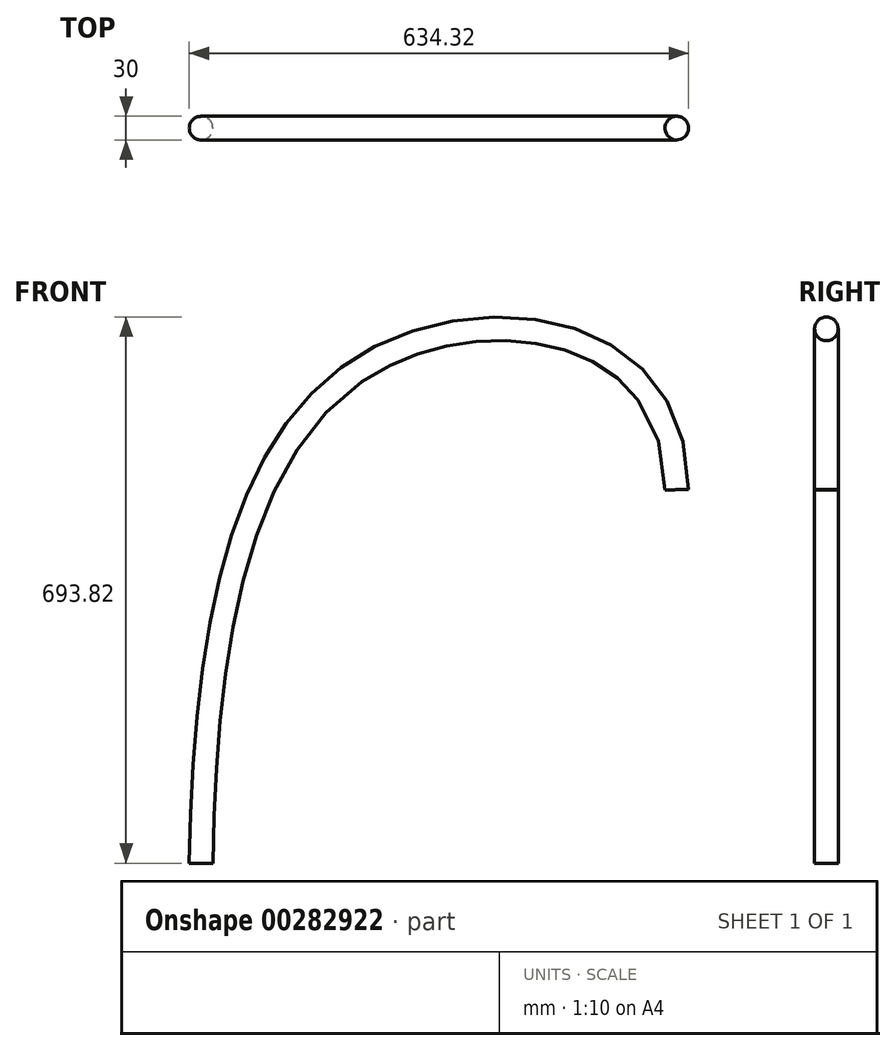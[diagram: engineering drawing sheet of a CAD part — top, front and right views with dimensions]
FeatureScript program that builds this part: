
annotation { "Feature Type Name" : "Feature", "Feature Type Description" : "" }
export const myFeature = defineFeature(function(context is Context, id is Id, definition is map)
    precondition{}
    {
        {
            var Q0;
            Q0=qCreatedBy(makeId("Front.planeOp"),FACE);
            var sketch = newSketch(context, id + "F0", { "sketchPlane" : qUnion([Q0])});
            skFitSpline(sketch, "E0", {"points": [v(0, 0) * mm, v(-380.97, 166.33) * mm, v(-604.32, -474.46) * mm], "startDerivative": vector(0, 1443.01) * mm, "endDerivative": vector(-27.43, -1426.3) * mm});
            skFitSpline(sketch, "E1.0", {"points": [v(-10, 0) * mm, v(-10, 14.5) * mm, v(-12.31, 41.6) * mm, v(-21.9, 76.83) * mm, v(-36.86, 106.96) * mm, v(-56.54, 132.32) * mm, v(-80.38, 153.2) * mm, v(-107.82, 169.76) * mm, v(-138.25, 182.1) * mm, v(-170.98, 190.29) * mm, v(-205.32, 194.42) * mm, v(-240.53, 194.62) * mm, v(-275.86, 191) * mm, v(-310.59, 183.71) * mm, v(-338.4, 174.72) * mm, v(-359.62, 165.86) * mm, v(-374.91, 158.41) * mm, v(-389.5, 150.17) * mm, v(-408.1, 138.15) * mm, v(-429.71, 121.23) * mm, v(-453.24, 98.05) * mm, v(-481.55, 63.5) * mm, v(-511.53, 13.9) * mm, v(-539.67, -54.5) * mm, v(-560.85, -130.24) * mm, v(-575.98, -211.72) * mm, v(-586, -297.36) * mm, v(-591.9, -385.56) * mm, v(-593.75, -445.02) * mm, v(-594.32, -474.65) * mm]});
            skFitSpline(sketch, "E2.0", {"points": [v(10, 0) * mm, v(10, 15.56) * mm, v(7.52, 44.95) * mm, v(-3.05, 83.88) * mm, v(-19.78, 117.62) * mm, v(-41.91, 146.14) * mm, v(-68.57, 169.48) * mm, v(-98.9, 187.76) * mm, v(-132.1, 201.2) * mm, v(-167.4, 210.02) * mm, v(-204.1, 214.43) * mm, v(-241.51, 214.63) * mm, v(-278.95, 210.8) * mm, v(-315.72, 203.08) * mm, v(-345.24, 193.54) * mm, v(-367.85, 184.1) * mm, v(-381.48, 177.46) * mm, v(-392.04, 171.72) * mm, v(-402.36, 165.69) * mm, v(-414.81, 157.63) * mm, v(-429.06, 147.15) * mm, v(-447.15, 132.15) * mm, v(-468.06, 111.53) * mm, v(-490.59, 84.04) * mm, v(-510.67, 54.04) * mm, v(-534.4, 10.96) * mm, v(-558.67, -48.12) * mm, v(-580.38, -125.82) * mm, v(-595.78, -208.8) * mm, v(-605.93, -295.58) * mm, v(-611.89, -384.62) * mm, v(-613.75, -444.47) * mm, v(-614.32, -474.27) * mm]});
            skLineSegment(sketch, "E3", {"start": v(-604.32, -474.46) * mm, "end": v(-242.7, -474.46) * mm, "construction": true});
            skLineSegment(sketch, "E4", {"start": v(-604.32, -474.46) * mm, "end": v(-604.32, -508.87) * mm, "construction": true});
            skSolve(sketch);
        }
        {
            var Q0;
            Q0=sQuery(id+"F0.wireOp",VERTEX,"E0.2.internal");
            var Q1;
            Q1=sQuery(id+"F0.wireOp",EDGE,"E4");
            cPlane(context, id + "F1", {"entities" : qUnion([Q0, Q1]), "cplaneType" : CPlaneType.LINE_POINT, "offset" : 25 * mm, "width" : 150 * mm, "height" : 150 * mm});
        }
        {
            var Q0;
            Q0=qCreatedBy(id+"F1.planeOp",FACE);
            var sketch = newSketch(context, id + "F2", { "sketchPlane" : qUnion([Q0])});
            skCircle(sketch, "E5", {"center": v(-604.32, 0) * mm, "radius": 15 * mm});
            skSolve(sketch);
        }
        {
            var Q0;
            Q0 = qSketchRegion(id + "F2", true);
            var Q1;
            Q1=sQuery(id+"F0.wireOp",EDGE,"E0");
            sweep(context, id + "F3", {"profiles" : qUnion([Q0]), "path" : qUnion([Q1])});
        }
    });
